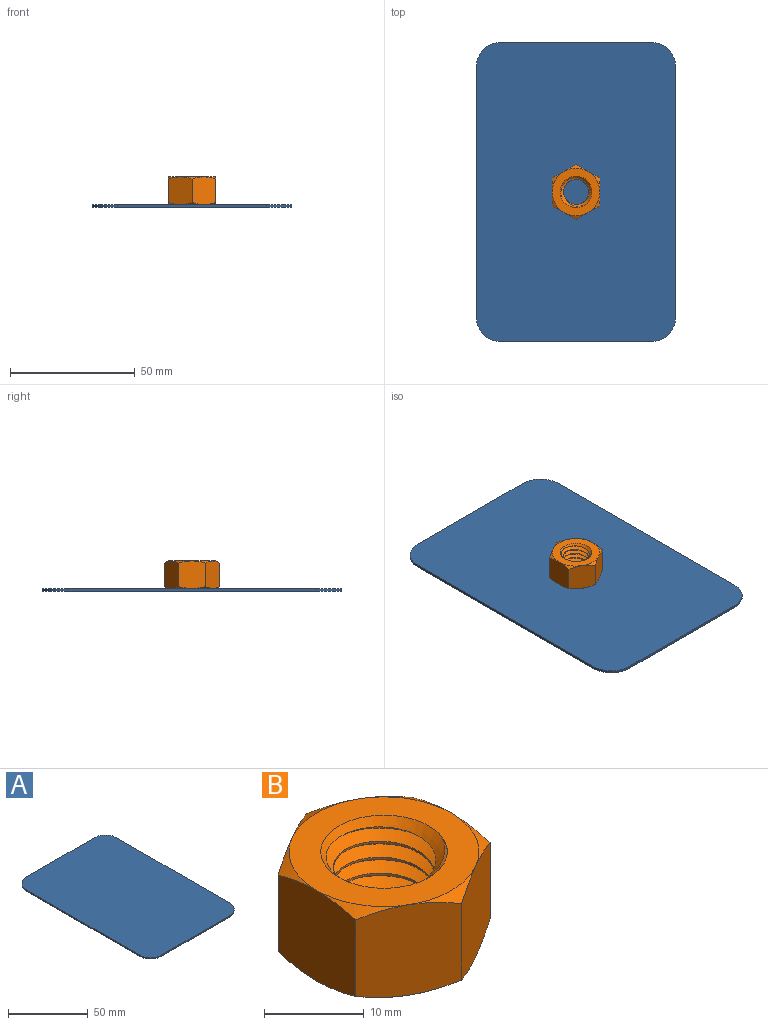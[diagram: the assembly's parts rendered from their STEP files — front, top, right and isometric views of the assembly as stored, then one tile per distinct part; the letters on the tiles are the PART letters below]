
ASSEMBLY  parts=2 mates=1
PART A: 10 faces, bbox 80x120x1 mm
  f0: plane 60x1mm, normal (0,1,0), area 60mm2, adj f1,f7,f8,f9
  f1: cylinder r=10mm len=10mm, axis (0,0,-1), area 15.7mm2, adj f0,f2,f8,f9
  f2: plane 100x1mm, normal (-1,0,0), area 100mm2, adj f1,f3,f8,f9
  f3: cylinder r=10mm len=10mm, axis (0,0,-1), area 15.7mm2, adj f2,f4,f8,f9
  f4: plane 60x1mm, normal (0,-1,0), area 60mm2, adj f3,f5,f8,f9
  f5: cylinder r=10mm len=10mm, axis (0,0,-1), area 15.7mm2, adj f4,f6,f8,f9
  f6: plane 100x1mm, normal (1,0,0), area 100mm2, adj f5,f7,f8,f9
  f7: cylinder r=10mm len=10mm, axis (0,0,-1), area 15.7mm2, adj f0,f6,f8,f9
  f8: plane 120x80mm, normal (0,0,1), area 9514.2mm2, adj f0,f1,f2,f3,f4,f5,f6,f7
  f9: plane 120x80mm, normal (0,0,-1), area 9514.2mm2, adj f0,f1,f2,f3,f4,f5,f6,f7
PART B: 26 faces, bbox 22.9x22.9x13.5 mm
  f0: cone r=5.86mm half-angle=45deg, axis (0,0,-1), area 33.1mm2, adj f10,f11,f12,f13
  f1: cone r=5.86mm half-angle=45deg, axis (0,0,1), area 33.1mm2, adj f3,f11,f12,f13
  f2: cylinder r=6.35mm len=12.7mm, axis (0,0,-1), area 55.4mm2, adj f3,f10,f11,f13
  f3: plane 19.05x19.05mm, normal (0,0,1), area 158.3mm2, adj f1,f2,f14,f15,f16,f17,f18,f19
  f4: plane 12.02x10.43mm, normal (-0.5,0.87,0), area 115.8mm2, adj f5,f9,f14,f19,f21,f22
  f5: plane 12.02x11.91mm, normal (-1,0,0), area 115.8mm2, adj f4,f6,f18,f19,f22,f23
  f6: plane 12.02x10.43mm, normal (-0.5,-0.87,0), area 115.8mm2, adj f5,f7,f17,f18,f23,f24
  f7: plane 12.02x10.43mm, normal (0.5,-0.87,0), area 115.8mm2, adj f6,f8,f16,f17,f24,f25
  f8: plane 12.02x11.91mm, normal (1,0,0), area 115.8mm2, adj f7,f9,f15,f16,f20,f25
  f9: plane 12.02x10.43mm, normal (0.5,0.87,0), area 115.8mm2, adj f4,f8,f14,f15,f20,f21
  f10: plane 19.05x19.05mm, normal (0,0,-1), area 158.3mm2, adj f0,f2,f20,f21,f22,f23,f24,f25
  f11: bspline ~12.69x12.69mm, area 272.1mm2, adj f0,f1,f2,f12
  f12: bspline ~10.69x10.16mm, area 34.2mm2, adj f0,f1,f11,f13
  f13: bspline ~12.69x12.69mm, area 267.1mm2, adj f0,f1,f2,f12
  f14: cone r=9.53mm half-angle=60deg, axis (0,0,-1), area 8.9mm2, adj f3,f4,f9
  f15: cone r=9.53mm half-angle=60deg, axis (0,0,-1), area 8.9mm2, adj f3,f8,f9
  f16: cone r=9.53mm half-angle=60deg, axis (0,0,-1), area 8.9mm2, adj f3,f7,f8
  f17: cone r=9.53mm half-angle=60deg, axis (0,0,-1), area 8.9mm2, adj f3,f6,f7
  f18: cone r=9.53mm half-angle=60deg, axis (0,0,-1), area 8.9mm2, adj f3,f5,f6
  f19: cone r=9.53mm half-angle=60deg, axis (0,0,-1), area 8.9mm2, adj f3,f4,f5
  f20: cone r=9.53mm half-angle=60deg, axis (0,0,1), area 8.9mm2, adj f8,f9,f10
  f21: cone r=9.53mm half-angle=60deg, axis (0,0,1), area 8.9mm2, adj f4,f9,f10
  f22: cone r=9.53mm half-angle=60deg, axis (0,0,1), area 8.9mm2, adj f4,f5,f10
  f23: cone r=9.53mm half-angle=60deg, axis (0,0,1), area 8.9mm2, adj f5,f6,f10
  f24: cone r=9.53mm half-angle=60deg, axis (0,0,1), area 8.9mm2, adj f6,f7,f10
  f25: cone r=9.53mm half-angle=60deg, axis (0,0,1), area 8.9mm2, adj f7,f8,f10
PLACE A t=(-1.9,3.5,0)mm
PLACE B rot(axis=(1,0,0),180deg) t=(38.1,63.5,6.56)mm
MATE fastened B.f2 <-> A.f8  axis (0,0,-1) through (38.1,63.5,1)mm
